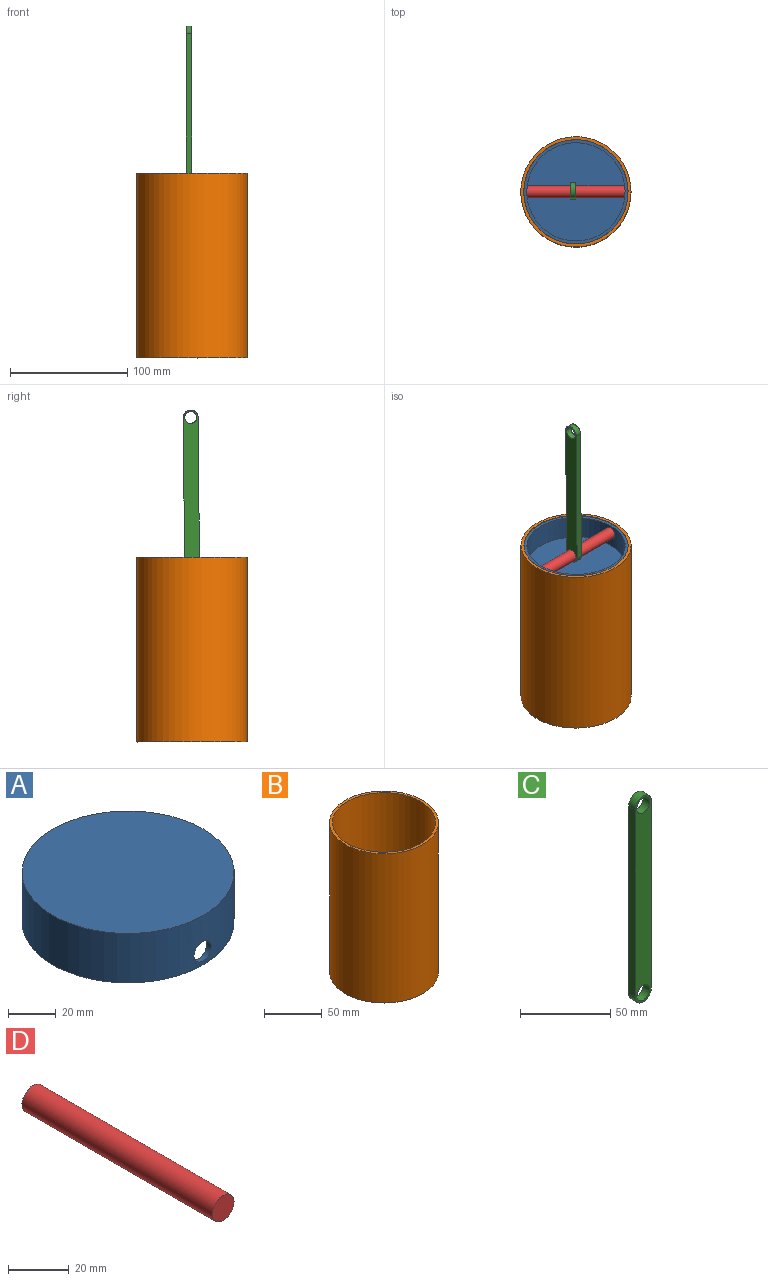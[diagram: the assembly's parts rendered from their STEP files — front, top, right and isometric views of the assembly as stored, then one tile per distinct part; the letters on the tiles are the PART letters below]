
ASSEMBLY  parts=4 mates=3
PART A: 7 faces, bbox 88.9x88.9x25.4 mm
  f0: cylinder r=41.91mm len=83.82mm, axis (0,0,-1), area 5187.7mm2, adj f3,f4,f5,f6
  f1: cylinder r=44.45mm len=88.9mm, axis (0,0,-1), area 6930.9mm2, adj f2,f3,f5,f6
  f2: plane 88.9x88.9mm, normal (0,0,1), area 6207.2mm2, adj f1
  f3: plane 88.9x88.9mm, normal (0,0,-1), area 689.1mm2, adj f0,f1
  f4: plane 83.82x83.82mm, normal (0,0,-1), area 5518mm2, adj f0
  f5: cylinder r=5.08mm len=10.16mm, axis (0,1,0), area 81.4mm2, adj f0,f1
  f6: cylinder r=5.08mm len=10.16mm, axis (0,1,0), area 81.4mm2, adj f0,f1
PART B: 5 faces, bbox 94x94x157.5 mm
  f0: cylinder r=44.45mm len=152.4mm, axis (0,0,-1), area 42563.4mm2, adj f2,f3
  f1: cylinder r=46.99mm len=157.48mm, axis (0,0,-1), area 46495.5mm2, adj f2,f4
  f2: plane 93.98x93.98mm, normal (0,0,1), area 729.7mm2, adj f0,f1
  f3: plane 88.9x88.9mm, normal (0,0,1), area 6207.2mm2, adj f0
  f4: plane 93.98x93.98mm, normal (0,0,-1), area 6936.8mm2, adj f1
PART C: 8 faces, bbox 12.7x5.1x139.7 mm
  f0: plane 127x5.08mm, normal (1,0,0), area 645.2mm2, adj f1,f4,f6,f7
  f1: cylinder r=6.35mm len=12.7mm, axis (0,1,0), area 101.3mm2, adj f0,f2,f6,f7
  f2: plane 127x5.08mm, normal (-1,0,0), area 645.2mm2, adj f1,f4,f6,f7
  f3: cylinder r=5.08mm len=10.16mm, axis (0,1,0), area 162.1mm2, adj f6,f7
  f4: cylinder r=6.35mm len=12.7mm, axis (0,1,0), area 101.3mm2, adj f0,f2,f6,f7
  f5: cylinder r=5.08mm len=10.16mm, axis (0,1,0), area 162.1mm2, adj f6,f7
  f6: plane 139.7x12.7mm, normal (0,-1,0), area 1577.4mm2, adj f0,f1,f2,f3,f4,f5
  f7: plane 139.7x12.7mm, normal (0,1,0), area 1577.4mm2, adj f0,f1,f2,f3,f4,f5
PART D: 3 faces, bbox 10.2x88.9x10.2 mm
  f0: cylinder r=5.08mm len=88.9mm, axis (0,1,0), area 2837.6mm2, adj f1,f2
  f1: plane 10.16x10.16mm, normal (0,-1,0), area 81.1mm2, adj f0
  f2: plane 10.16x10.16mm, normal (0,1,0), area 81.1mm2, adj f0
PLACE A rot(axis=(0.71,-0.71,0),180deg) t=(-117.94,9.46,225.66)mm
PLACE B rot(axis=(-0.99,0.06,-0.12),0deg) t=(-117.94,9.46,73.78)mm fixed
PLACE C rot(axis=(0,0,1),90deg) t=(-123,9.85,265.17)mm fixed
PLACE D rot(axis=(0.58,-0.58,0.58),120deg) t=(-162.37,25.11,218.53)mm
MATE revolute C.f3 <-> D.f0  axis (-1,0,0) through (-117.92,9.46,218.53)mm
MATE fastened D.f0 <-> A.f5  axis (1,0,0) through (-73.47,9.46,218.53)mm
MATE slider A.f1 <-> B.f0  axis (0,0,-1) through (-117.94,9.46,200.26)mm
